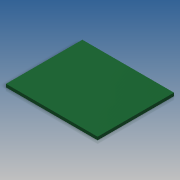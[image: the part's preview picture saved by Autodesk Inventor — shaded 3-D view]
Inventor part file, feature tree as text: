
AUTODESK INVENTOR PART (.ipt)
format: ipt  version: 2016 SP2 (Build 200236200, 236)  size: 91,136 bytes
history: native  units: in
note: dims shown in document units (in); Inventor stores cm internally (conversion verified against a paired STEP export)
features: extrude x1, sketch x1
ambient origin geometry x8: Origin, YZ Plane, XZ Plane, XY Plane, X Axis, Y Axis, Z Axis, Center Point
bodies: Solid1 (feature_tree)
feature tree (2):
  extrude  "Extrusion1"  Depth=1.8898in
  sketch  "Sketch2"  dims[d0=1.5748in d1=1.8898in d2=0.063in d3=0.0in]
